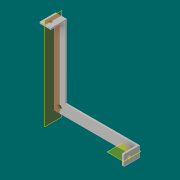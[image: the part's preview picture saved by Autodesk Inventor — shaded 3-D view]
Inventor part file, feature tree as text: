
AUTODESK INVENTOR PART (.ipt)
format: ipt  version: 2016 (Build 200138000, 138)  size: 131,072 bytes
history: native  units: in
note: dims shown in document units (in); Inventor stores cm internally (conversion verified against a paired STEP export)
features: extrude x4, sketch x4, plane x2, fillet x1, pattern_circular x1
ambient origin geometry x8: Origin, YZ Plane, XZ Plane, XY Plane, X Axis, Y Axis, Z Axis, Center Point
bodies: Solid1 (feature_tree)
feature tree (12):
  extrude  "Extrusion1"  Depth=0.6in
  extrude  "Extrusion2"  Depth=0.08in
  extrude  "Extrusion3"  Depth=0.3in
  fillet  "Fillet1"  Radius=0.16in
  plane  "Work Plane1"
  extrude  "Extrusion4"  Depth=0.05in
  pattern_circular  "Circular Pattern1"  [2 undecoded]
  plane  "Work Plane2"
  sketch  "Sketch1"  dims[d0=0.87in d1=0.6in]
  sketch  "Sketch2"  dims[d2=0.08in d3=0.0in d4=0.08in]
  sketch  "Sketch3"  dims[d5=0.75in d6=0.0in d7=0.3in d8=0.16in]
  sketch  "Sketch4"  dims[d9=0.75in d10=0.0in d11=0.05in d12=0.25in d13=0.6in d14=4.3in d15=3.47in d16=0.0in d17=0.0in d18=0.7874in d19=-0.6184in]
note: 2 required parameter values undecoded (feature->parameter linkage not recoverable at this tier; creation-order binding heuristic only, values carry confidence <= 0.55)
